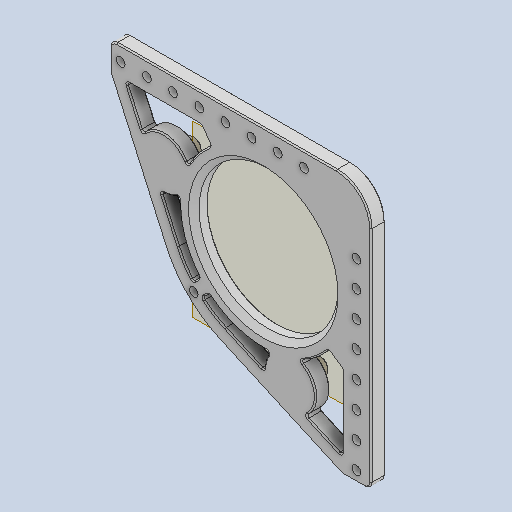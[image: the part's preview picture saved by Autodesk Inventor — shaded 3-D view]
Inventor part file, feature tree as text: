
AUTODESK INVENTOR PART (.ipt)
format: ipt  version: 2022 (Build 260153000, 153)  size: 920,576 bytes
history: native  units: in
note: dims shown in document units (in); Inventor stores cm internally (conversion verified against a paired STEP export)
features: chamfer x5, extrude x4, sketch x3, other x3, fillet x2, plane x1, pattern_circular x1, reference x1, projected_geometry x1
ambient origin geometry x8: Origin, YZ Plane, XZ Plane, XY Plane, X Axis, Y Axis, Z Axis, Center Point
bodies: Solid1 (feature_tree)
feature tree (21):
  plane  "Work Plane1"
  extrude  "Extrusion1"  Depth=0.55in
  fillet  "Fillet1"  [1 undecoded]
  chamfer  "Chamfer1"  Distance=0.3937in
  chamfer  "Chamfer2"  Distance=4.7in
  chamfer  "Chamfer3"  Distance=0.2756in
  extrude  "Extrusion4"  Depth=0.125in
  extrude  "Extrusion5"  Depth=0.125in TaperAngle=45.0deg
  chamfer  "Chamfer5"  Distance=0.125in Angle=45.0deg
  pattern_circular  "Circular Pattern1"  Angle=45.0deg  [1 undecoded]
  extrude  "Extrusion6"  Depth=0.125in
  fillet  "Fillet3"  Radius=0.9449in
  chamfer  "Chamfer6"  Distance=1.1811in
  reference  "Reference1"
  sketch  "Sketch4"  dims[d0=0.1713in d11=0.55in d12=45.0deg]
  sketch  "Sketch5"  dims[d13=0.1679in]
  sketch  "Sketch6"  dims[d14=3.0in d15=1.5748in d17=0.5in d18=0.3937in d20=1.0in d23=4.7in d24=0.2756in d25=0.0in d26=0.125in d27=0.1in d28=0.125in d29=45.0deg d30=0.0236in d31=0.125in d32=45.0deg d33=0.0236in d34=0.125in d35=45.0deg d47=0.0059in d48=0.9449in d49=1.1811in d50=0.311in d51=0.315in d52=0.0in d53=0.4764in d54=0.1181in d55=0.0in d56=0.0236in d57=0.125in d58=45.0deg d59=1.1811in d60=360.0deg d62=0.25in d63=0.25in d64=0.25in d65=0.55in d66=0.55in d67=0.25in d68=0.25in d69=45.0deg d70=0.25in d71=0.0in d72=0.0in d73=0.0394in d74=0.0236in d75=0.125in d76=45.0deg d89=1.9685in d91=0.5in d92=0.3937in d94=1.0in d96=0.1679in d99=0.125in]
  projected_geometry  "Projected Loop10"
  other  "<userpath>\Documents\CAD\guardSwerve1\Assembly1.iam"
  other  "Assembly1.iam"
  other  "Undercarriage:1"
note: 2 required parameter values undecoded (feature->parameter linkage not recoverable at this tier; creation-order binding heuristic only, values carry confidence <= 0.55)
